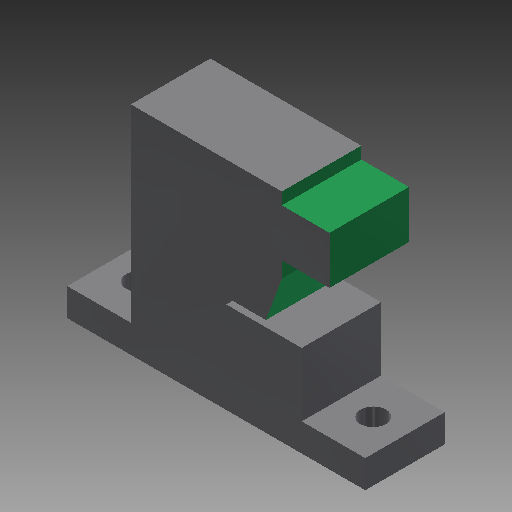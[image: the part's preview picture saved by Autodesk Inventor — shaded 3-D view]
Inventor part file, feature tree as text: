
AUTODESK INVENTOR PART (.ipt)
format: ipt  version: 2018 (Build 220112000, 112)  size: 132,608 bytes
history: native  units: mm
features: hole x2, extrude x1
ambient origin geometry x8: Origin, YZ Plane, XZ Plane, XY Plane, X Axis, Y Axis, Z Axis, Center Point
bodies: Volumenkörper1 (feature_tree)
feature tree (3):
  extrude  "Extrusion1"  Depth=27.3mm
  hole  "Bohrung1"  [1 undecoded]
  hole  "Bohrung2"  [1 undecoded]
note: 2 required parameter values undecoded (feature->parameter linkage not recoverable at this tier; creation-order binding heuristic only, values carry confidence <= 0.55)
